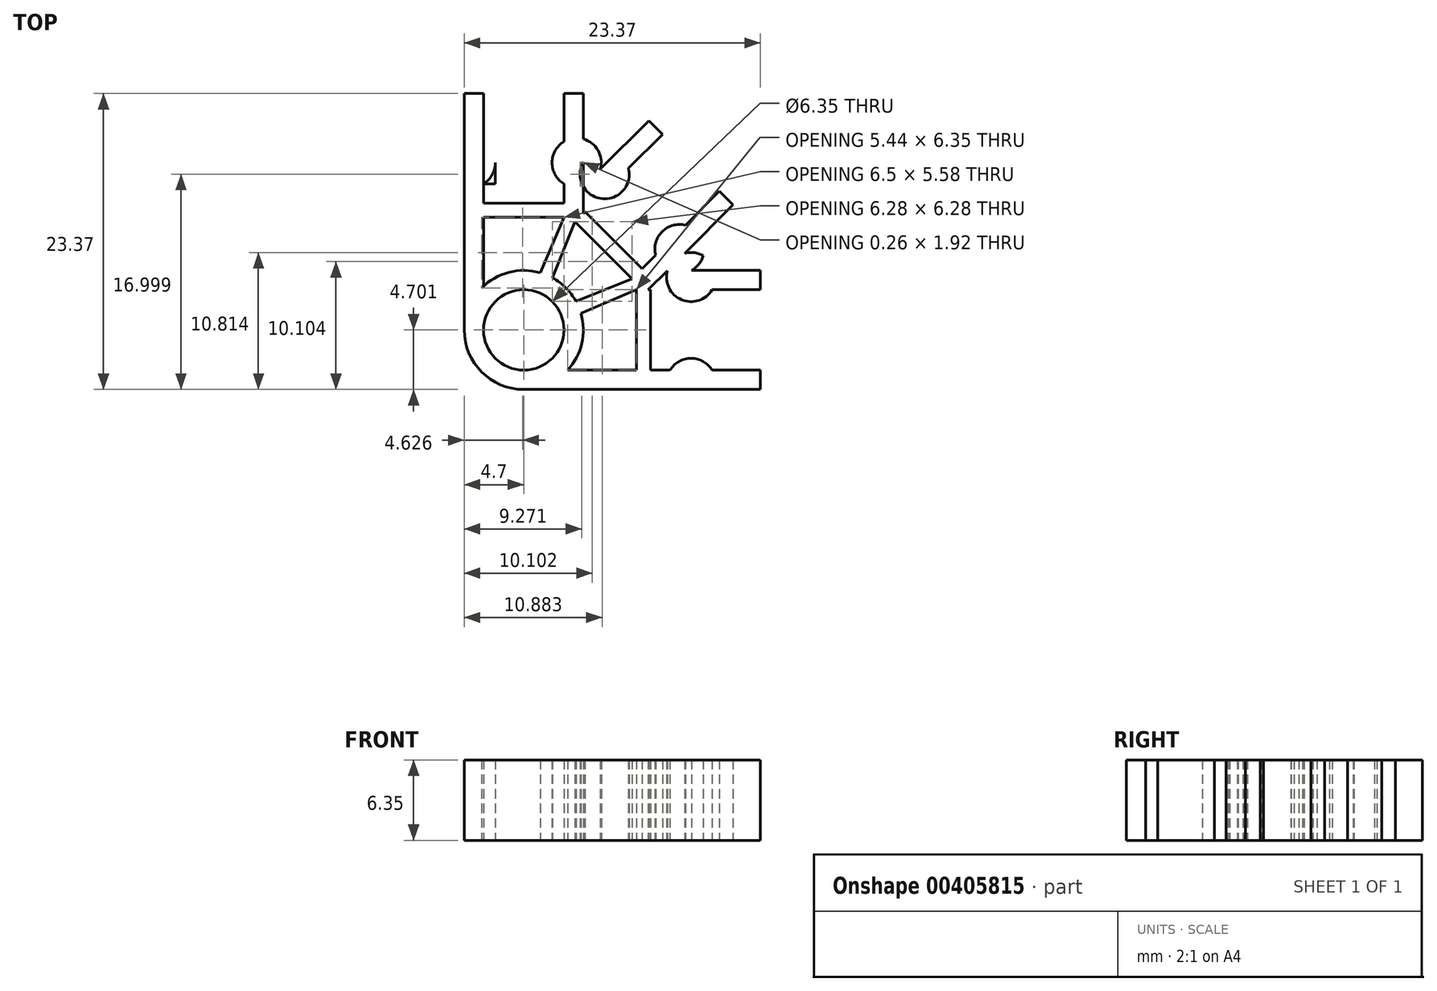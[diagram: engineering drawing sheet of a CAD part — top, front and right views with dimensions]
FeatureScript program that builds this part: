
annotation { "Feature Type Name" : "Feature", "Feature Type Description" : "" }
export const myFeature = defineFeature(function(context is Context, id is Id, definition is map)
    precondition{}
    {
        {
            var Q0;
            Q0=qCreatedBy(makeId("Top.planeOp"),FACE);
            var sketch = newSketch(context, id + "F0", { "sketchPlane" : qUnion([Q0])});
            skLineSegment(sketch, "E0", {"start": v(0, 8.65) * mm, "end": v(0, -8.65) * mm});
            skLineSegment(sketch, "E1.bottom", {"start": v(-3.17, 8.65) * mm, "end": v(3.18, 8.65) * mm});
            skLineSegment(sketch, "E1.top", {"start": v(-3.17, -8.65) * mm, "end": v(3.18, -8.65) * mm});
            skLineSegment(sketch, "E1.left", {"start": v(-3.18, 8.65) * mm, "end": v(-3.18, -8.65) * mm});
            skLineSegment(sketch, "E1.right", {"start": v(3.18, 8.65) * mm, "end": v(3.18, -8.65) * mm});
            skPoint(sketch, "E1.middle", {"position": v(0, 0) * mm});
            skLineSegment(sketch, "E2", {"start": v(-3.18, -7.12) * mm, "end": v(3.18, -7.12) * mm});
            skLineSegment(sketch, "E3", {"start": v(-3.18, -3.8) * mm, "end": v(3.18, -3.8) * mm});
            skLineSegment(sketch, "E4.bottom", {"start": v(-2.24, 8.65) * mm, "end": v(2.24, 8.65) * mm});
            skLineSegment(sketch, "E4.top", {"start": v(-2.24, -8.65) * mm, "end": v(2.24, -8.65) * mm});
            skLineSegment(sketch, "E4.left", {"start": v(-2.24, 8.65) * mm, "end": v(-2.24, -8.65) * mm});
            skLineSegment(sketch, "E4.right", {"start": v(2.24, 8.65) * mm, "end": v(2.24, -8.65) * mm});
            skCircle(sketch, "E5", {"center": v(4.18, -5.46) * mm, "radius": 1.94 * mm});
            skPoint(sketch, "E5.third.point", {"position": v(2.24, -5.46) * mm});
            skLineSegment(sketch, "E6.MirrorCS", {"start": v(3.17, -8.65) * mm, "end": v(-3.18, -8.65) * mm});
            skLineSegment(sketch, "E7.MirrorCS", {"start": v(3.17, 8.65) * mm, "end": v(-3.18, 8.65) * mm});
            skPoint(sketch, "E8.MirrorP", {"position": v(-2.24, -5.46) * mm});
            skLineSegment(sketch, "E9.MirrorCS", {"start": v(2.24, -8.65) * mm, "end": v(-2.24, -8.65) * mm});
            skLineSegment(sketch, "E10.MirrorCS", {"start": v(2.24, 8.65) * mm, "end": v(-2.24, 8.65) * mm});
            skLineSegment(sketch, "E11.MirrorCS", {"start": v(3.18, -7.12) * mm, "end": v(-3.18, -7.12) * mm});
            skLineSegment(sketch, "E12.MirrorCS", {"start": v(3.18, -3.8) * mm, "end": v(-3.18, -3.8) * mm});
            skCircle(sketch, "E13.MirrorC", {"center": v(-4.18, -5.46) * mm, "radius": 1.94 * mm});
            skLineSegment(sketch, "E14.MirrorCS", {"start": v(-3.18, 3.8) * mm, "end": v(3.18, 3.8) * mm});
            skLineSegment(sketch, "E15.MirrorCS", {"start": v(3.18, 7.12) * mm, "end": v(-3.18, 7.12) * mm});
            skLineSegment(sketch, "E16.MirrorCS", {"start": v(3.18, 3.8) * mm, "end": v(-3.18, 3.8) * mm});
            skLineSegment(sketch, "E17.MirrorCS", {"start": v(2.24, -8.65) * mm, "end": v(2.24, 8.65) * mm});
            skLineSegment(sketch, "E18.MirrorCS", {"start": v(-2.24, -8.65) * mm, "end": v(-2.24, 8.65) * mm});
            skLineSegment(sketch, "E19.MirrorCS", {"start": v(-3.18, 7.12) * mm, "end": v(3.17, 7.12) * mm});
            skLineSegment(sketch, "E20.MirrorCS", {"start": v(3.18, -8.65) * mm, "end": v(3.17, 8.65) * mm});
            skLineSegment(sketch, "E21.MirrorCS", {"start": v(0, -8.65) * mm, "end": v(0, 8.65) * mm});
            skLineSegment(sketch, "E22.MirrorCS", {"start": v(-3.18, -8.65) * mm, "end": v(-3.18, 8.65) * mm});
            skCircle(sketch, "E23.MirrorC", {"center": v(-4.18, 5.46) * mm, "radius": 1.94 * mm});
            skCircle(sketch, "E24.MirrorC", {"center": v(4.18, 5.46) * mm, "radius": 1.94 * mm});
            skLineSegment(sketch, "E25.MirrorCS", {"start": v(-3.17, -8.65) * mm, "end": v(-3.17, 8.65) * mm});
            skPoint(sketch, "E26.MirrorP", {"position": v(-2.24, 5.46) * mm});
            skLineSegment(sketch, "E27.MirrorCS", {"start": v(3.18, -8.65) * mm, "end": v(3.18, 8.65) * mm});
            skPoint(sketch, "E28.MirrorP", {"position": v(2.24, 5.46) * mm});
            skLineSegment(sketch, "E29.bottom", {"start": v(-4.7, 0) * mm, "end": v(4.7, 0) * mm});
            skLineSegment(sketch, "E29.top", {"start": v(-4.7, -23.37) * mm, "end": v(4.7, -23.37) * mm});
            skLineSegment(sketch, "E29.left", {"start": v(-4.7, 0) * mm, "end": v(-4.7, -23.37) * mm});
            skLineSegment(sketch, "E29.right", {"start": v(4.7, 0) * mm, "end": v(4.7, -23.37) * mm});
            skCircle(sketch, "E30", {"center": v(0, -18.67) * mm, "radius": 3.18 * mm});
            skCircle(sketch, "E31", {"center": v(0, -18.67) * mm, "radius": 4.7 * mm});
            skLineSegment(sketch, "E32", {"start": v(-4.7, -9.77) * mm, "end": v(4.7, -9.77) * mm});
            skLineSegment(sketch, "E33", {"start": v(3.18, -8.65) * mm, "end": v(3.18, -18.67) * mm});
            skLineSegment(sketch, "E34", {"start": v(-3.17, -8.65) * mm, "end": v(-3.17, -18.67) * mm});
            skLineSegment(sketch, "E35.1.0", {"start": v(9.88, -2.15) * mm, "end": v(16.52, -8.8) * mm});
            skLineSegment(sketch, "E35.1.1", {"start": v(9.88, -2.15) * mm, "end": v(-6.65, -18.67) * mm});
            skLineSegment(sketch, "E35.1.2", {"start": v(17.07, 2.9) * mm, "end": v(4.84, -9.34) * mm});
            skLineSegment(sketch, "E35.1.3", {"start": v(9.33, -13.83) * mm, "end": v(4.84, -9.34) * mm});
            skLineSegment(sketch, "E35.1.4", {"start": v(2.97, -9.05) * mm, "end": v(9.62, -15.7) * mm});
            skLineSegment(sketch, "E35.1.5", {"start": v(4.84, -9.34) * mm, "end": v(-2.25, -16.42) * mm});
            skLineSegment(sketch, "E35.1.6", {"start": v(9.33, -13.83) * mm, "end": v(2.25, -20.91) * mm});
            skLineSegment(sketch, "E35.1.9", {"start": v(16.52, -8.8) * mm, "end": v(0, -25.31) * mm});
            skLineSegment(sketch, "E35.1.10", {"start": v(21.56, -1.6) * mm, "end": v(9.33, -13.83) * mm});
            skLineSegment(sketch, "E35.2.0", {"start": v(18.67, -13.97) * mm, "end": v(18.67, -23.37) * mm});
            skLineSegment(sketch, "E35.2.1", {"start": v(18.67, -13.97) * mm, "end": v(-4.7, -13.97) * mm});
            skLineSegment(sketch, "E35.2.2", {"start": v(27.32, -15.5) * mm, "end": v(10.02, -15.5) * mm});
            skLineSegment(sketch, "E35.2.3", {"start": v(10.02, -21.84) * mm, "end": v(10.02, -15.5) * mm});
            skLineSegment(sketch, "E35.2.4", {"start": v(8.9, -13.97) * mm, "end": v(8.9, -23.37) * mm});
            skLineSegment(sketch, "E35.2.5", {"start": v(10.02, -15.5) * mm, "end": v(0, -15.5) * mm});
            skLineSegment(sketch, "E35.2.6", {"start": v(10.02, -21.84) * mm, "end": v(0, -21.84) * mm});
            skLineSegment(sketch, "E35.2.9", {"start": v(18.67, -23.37) * mm, "end": v(-4.7, -23.37) * mm});
            skLineSegment(sketch, "E35.2.10", {"start": v(27.32, -21.84) * mm, "end": v(10.02, -21.84) * mm});
            skLineSegment(sketch, "E35.anchor1", {"start": v(0, -18.67) * mm, "end": v(-4.7, 0) * mm, "construction": true});
            skLineSegment(sketch, "E35.anchor2", {"start": v(0, -18.67) * mm, "end": v(18.67, -13.97) * mm, "construction": true});
            skCircle(sketch, "E36", {"center": v(0, -18.67) * mm, "radius": 0.56 * mm});
            skLineSegment(sketch, "E37", {"start": v(3.17, -9.77) * mm, "end": v(-0.51, -18.45) * mm});
            skLineSegment(sketch, "E38", {"start": v(4.05, -10.13) * mm, "end": v(0.52, -18.88) * mm});
            skLineSegment(sketch, "E39", {"start": v(8.54, -14.62) * mm, "end": v(-0.2, -18.15) * mm});
            skLineSegment(sketch, "E40", {"start": v(8.9, -15.5) * mm, "end": v(0.22, -19.18) * mm});
            skCircle(sketch, "E41.1.0", {"center": v(6.39, -6.38) * mm, "radius": 1.94 * mm});
            skCircle(sketch, "E41.1.1", {"center": v(12.3, -12.28) * mm, "radius": 1.94 * mm});
            skCircle(sketch, "E41.2.0", {"center": v(13.2, -14.5) * mm, "radius": 1.94 * mm});
            skCircle(sketch, "E41.2.1", {"center": v(13.2, -22.85) * mm, "radius": 1.94 * mm});
            skLineSegment(sketch, "E41.anchor1", {"start": v(0, -18.67) * mm, "end": v(-4.18, -5.46) * mm, "construction": true});
            skLineSegment(sketch, "E41.anchor2", {"start": v(0, -18.67) * mm, "end": v(13.2, -14.5) * mm, "construction": true});
            skSolve(sketch);
        }
        {
            var Q0;
            {var subQ3=sQuery(id+"F0.wireOp",EDGE,"E30");var subQ7=sQuery(id+"F0.wireOp",EDGE,"E34");var subQ8=makeQuery(id+"F0.imprint","INTERSECT",VERTEX,{"derivedFrom":[subQ7,subQ3]});Q0=makeQuery(id+"F0.imprint","IMPRINT",FACE,{"disambiguationData":[TD([[makeQuery(id+"F0.imprint","IMPRINT",EDGE,{"disambiguationData":[TD([[subQ8,1.0]])],"derivedFrom":subQ7}),-1.0]])]});}
            var Q1;
            {var subQ4=sQuery(id+"F0.wireOp",EDGE,"E30");var subQ5=sQuery(id+"F0.wireOp",EDGE,"E34");var subQ6=makeQuery(id+"F0.imprint","INTERSECT",VERTEX,{"derivedFrom":[subQ5,subQ4]});Q1=makeQuery(id+"F0.imprint","IMPRINT",FACE,{"disambiguationData":[TD([[makeQuery(id+"F0.imprint","IMPRINT",EDGE,{"disambiguationData":[TD([[subQ6,1.0]])],"derivedFrom":subQ5}),1.0]])]});}
            var Q2;
            {var subQ0=sQuery(id+"F0.wireOp",EDGE,"E30");var subQ1=sQuery(id+"F0.wireOp",EDGE,"E35.1.5");var subQ2=makeQuery(id+"F0.imprint","INTERSECT",VERTEX,{"derivedFrom":[subQ1,subQ0]});Q2=makeQuery(id+"F0.imprint","IMPRINT",FACE,{"disambiguationData":[TD([[makeQuery(id+"F0.imprint","IMPRINT",EDGE,{"disambiguationData":[TD([[subQ2,1.0]])],"derivedFrom":subQ1}),1.0]])]});}
            var Q3;
            {var subQ0=sQuery(id+"F0.wireOp",EDGE,"E30");var subQ1=sQuery(id+"F0.wireOp",EDGE,"E35.2.5");var subQ2=makeQuery(id+"F0.imprint","INTERSECT",VERTEX,{"derivedFrom":[subQ1,subQ0]});Q3=makeQuery(id+"F0.imprint","IMPRINT",FACE,{"disambiguationData":[TD([[makeQuery(id+"F0.imprint","IMPRINT",EDGE,{"disambiguationData":[TD([[subQ2,1.0]])],"derivedFrom":subQ1}),1.0]])]});}
            var Q4;
            {var subQ0=sQuery(id+"F0.wireOp",EDGE,"E38");var subQ1=sQuery(id+"F0.wireOp",EDGE,"E35.2.5");var subQ2=makeQuery(id+"F0.imprint","INTERSECT",VERTEX,{"derivedFrom":[subQ1,subQ0]});Q4=makeQuery(id+"F0.imprint","IMPRINT",FACE,{"disambiguationData":[TD([[makeQuery(id+"F0.imprint","IMPRINT",EDGE,{"disambiguationData":[TD([[subQ2,-1.0]])],"derivedFrom":subQ1}),1.0]])]});}
            var Q5;
            {var subQ0=sQuery(id+"F0.wireOp",EDGE,"E38");var subQ1=sQuery(id+"F0.wireOp",EDGE,"E35.2.5");var subQ2=makeQuery(id+"F0.imprint","INTERSECT",VERTEX,{"derivedFrom":[subQ1,subQ0]});Q5=makeQuery(id+"F0.imprint","IMPRINT",FACE,{"disambiguationData":[TD([[makeQuery(id+"F0.imprint","IMPRINT",EDGE,{"disambiguationData":[TD([[subQ2,-1.0]])],"derivedFrom":subQ1}),-1.0]])]});}
            var Q6;
            {var subQ0=sQuery(id+"F0.wireOp",EDGE,"E31");var subQ1=sQuery(id+"F0.wireOp",EDGE,"E33");var subQ2=makeQuery(id+"F0.imprint","INTERSECT",VERTEX,{"derivedFrom":[subQ1,subQ0]});Q6=makeQuery(id+"F0.imprint","IMPRINT",FACE,{"disambiguationData":[TD([[makeQuery(id+"F0.imprint","IMPRINT",EDGE,{"disambiguationData":[TD([[subQ2,-1.0]])],"derivedFrom":subQ1}),-1.0]])]});}
            var Q7;
            {var subQ1=sQuery(id+"F0.wireOp",EDGE,"E35.2.5");var subQ7=sQuery(id+"F0.wireOp",EDGE,"E33");var subQ8=makeQuery(id+"F0.imprint","INTERSECT",VERTEX,{"derivedFrom":[subQ7,subQ1]});Q7=makeQuery(id+"F0.imprint","IMPRINT",FACE,{"disambiguationData":[TD([[makeQuery(id+"F0.imprint","IMPRINT",EDGE,{"disambiguationData":[TD([[subQ8,-1.0]])],"derivedFrom":subQ7}),-1.0]])]});}
            var Q8;
            {var subQ0=sQuery(id+"F0.wireOp",EDGE,"E35.2.5");var subQ1=sQuery(id+"F0.wireOp",EDGE,"E33");var subQ2=makeQuery(id+"F0.imprint","INTERSECT",VERTEX,{"derivedFrom":[subQ1,subQ0]});Q8=makeQuery(id+"F0.imprint","IMPRINT",FACE,{"disambiguationData":[TD([[makeQuery(id+"F0.imprint","IMPRINT",EDGE,{"disambiguationData":[TD([[subQ2,-1.0]])],"derivedFrom":subQ1}),1.0]])]});}
            var Q9;
            {var subQ0=sQuery(id+"F0.wireOp",EDGE,"E39");var subQ1=sQuery(id+"F0.wireOp",EDGE,"E33");var subQ2=makeQuery(id+"F0.imprint","INTERSECT",VERTEX,{"derivedFrom":[subQ1,subQ0]});Q9=makeQuery(id+"F0.imprint","IMPRINT",FACE,{"disambiguationData":[TD([[makeQuery(id+"F0.imprint","IMPRINT",EDGE,{"disambiguationData":[TD([[subQ2,-1.0]])],"derivedFrom":subQ1}),-1.0]])]});}
            var Q10;
            {var subQ0=sQuery(id+"F0.wireOp",EDGE,"E39");var subQ1=sQuery(id+"F0.wireOp",EDGE,"E33");var subQ2=makeQuery(id+"F0.imprint","INTERSECT",VERTEX,{"derivedFrom":[subQ1,subQ0]});Q10=makeQuery(id+"F0.imprint","IMPRINT",FACE,{"disambiguationData":[TD([[makeQuery(id+"F0.imprint","IMPRINT",EDGE,{"disambiguationData":[TD([[subQ2,-1.0]])],"derivedFrom":subQ1}),1.0]])]});}
            var Q11;
            {var subQ0=sQuery(id+"F0.wireOp",EDGE,"E31");var subQ1=sQuery(id+"F0.wireOp",EDGE,"E33");var subQ2=makeQuery(id+"F0.imprint","INTERSECT",VERTEX,{"derivedFrom":[subQ1,subQ0]});Q11=makeQuery(id+"F0.imprint","IMPRINT",FACE,{"disambiguationData":[TD([[makeQuery(id+"F0.imprint","IMPRINT",EDGE,{"disambiguationData":[TD([[subQ2,-1.0]])],"derivedFrom":subQ1}),1.0]])]});}
            var Q12;
            {var subQ0=sQuery(id+"F0.wireOp",EDGE,"E30");var subQ1=sQuery(id+"F0.wireOp",EDGE,"E33");var subQ2=makeQuery(id+"F0.imprint","INTERSECT",VERTEX,{"derivedFrom":[subQ1,subQ0]});Q12=makeQuery(id+"F0.imprint","IMPRINT",FACE,{"disambiguationData":[TD([[makeQuery(id+"F0.imprint","IMPRINT",EDGE,{"disambiguationData":[TD([[subQ2,1.0]])],"derivedFrom":subQ1}),1.0]])]});}
            var Q13;
            {var subQ0=sQuery(id+"F0.wireOp",EDGE,"E30");var subQ1=sQuery(id+"F0.wireOp",EDGE,"E33");var subQ2=makeQuery(id+"F0.imprint","INTERSECT",VERTEX,{"derivedFrom":[subQ1,subQ0]});Q13=makeQuery(id+"F0.imprint","IMPRINT",FACE,{"disambiguationData":[TD([[makeQuery(id+"F0.imprint","IMPRINT",EDGE,{"disambiguationData":[TD([[subQ2,1.0]])],"derivedFrom":subQ1}),-1.0]])]});}
            var Q14;
            {var subQ4=sQuery(id+"F0.wireOp",EDGE,"E30");var subQ5=sQuery(id+"F0.wireOp",EDGE,"E35.1.6");var subQ6=makeQuery(id+"F0.imprint","INTERSECT",VERTEX,{"derivedFrom":[subQ5,subQ4]});Q14=makeQuery(id+"F0.imprint","IMPRINT",FACE,{"disambiguationData":[TD([[makeQuery(id+"F0.imprint","IMPRINT",EDGE,{"disambiguationData":[TD([[subQ6,1.0]])],"derivedFrom":subQ5}),1.0]])]});}
            var Q15;
            {var subQ0=sQuery(id+"F0.wireOp",EDGE,"E35.1.1");var subQ1=sQuery(id+"F0.wireOp",EDGE,"E29.left");var subQ2=makeQuery(id+"F0.imprint","INTERSECT",VERTEX,{"derivedFrom":[subQ1,subQ0]});Q15=makeQuery(id+"F0.imprint","IMPRINT",FACE,{"disambiguationData":[TD([[makeQuery(id+"F0.imprint","IMPRINT",EDGE,{"disambiguationData":[TD([[subQ2,-1.0]])],"derivedFrom":subQ1}),1.0]])]});}
            var Q16;
            {var subQ1=sQuery(id+"F0.wireOp",EDGE,"E29.left");var subQ4=sQuery(id+"F0.wireOp",EDGE,"E35.2.1");var subQ8=makeQuery(id+"F0.imprint","INTERSECT",VERTEX,{"derivedFrom":[subQ1,subQ4]});Q16=makeQuery(id+"F0.imprint","IMPRINT",FACE,{"disambiguationData":[TD([[makeQuery(id+"F0.imprint","IMPRINT",EDGE,{"disambiguationData":[TD([[subQ8,-1.0]])],"derivedFrom":subQ1}),1.0]])]});}
            var Q17;
            {var subQ0=sQuery(id+"F0.wireOp",EDGE,"E32");var subQ1=sQuery(id+"F0.wireOp",EDGE,"E29.left");var subQ2=makeQuery(id+"F0.imprint","INTERSECT",VERTEX,{"derivedFrom":[subQ1,subQ0]});Q17=makeQuery(id+"F0.imprint","IMPRINT",FACE,{"disambiguationData":[TD([[makeQuery(id+"F0.imprint","IMPRINT",EDGE,{"disambiguationData":[TD([[subQ2,-1.0]])],"derivedFrom":subQ1}),1.0]])]});}
            var Q18;
            {var subQ0=sQuery(id+"F0.wireOp",EDGE,"E32");var subQ1=sQuery(id+"F0.wireOp",EDGE,"E29.left");var subQ2=makeQuery(id+"F0.imprint","INTERSECT",VERTEX,{"derivedFrom":[subQ1,subQ0]});Q18=makeQuery(id+"F0.imprint","IMPRINT",FACE,{"disambiguationData":[TD([[makeQuery(id+"F0.imprint","IMPRINT",EDGE,{"disambiguationData":[TD([[subQ2,1.0]])],"derivedFrom":subQ1}),1.0]])]});}
            var Q19;
            {var subQ0=sQuery(id+"F0.wireOp",EDGE,"E13.MirrorC");var subQ4=sQuery(id+"F0.wireOp",EDGE,"E29.left");var subQ5=makeQuery(id+"F0.imprint","INTERSECT",VERTEX,{"disambiguationData":[OD(0.0)],"derivedFrom":[subQ0,subQ4]});Q19=makeQuery(id+"F0.imprint","IMPRINT",FACE,{"disambiguationData":[TD([[makeQuery(id+"F0.imprint","IMPRINT",EDGE,{"disambiguationData":[TD([[subQ5,-1.0]])],"derivedFrom":subQ4}),1.0]])]});}
            var Q20;
            {var subQ3=sQuery(id+"F0.wireOp",EDGE,"E29.bottom");var subQ5=sQuery(id+"F0.wireOp",EDGE,"E29.left");var subQ6=makeQuery(id+"F0.imprint","INTERSECT",VERTEX,{"derivedFrom":[subQ3,subQ5]});Q20=makeQuery(id+"F0.imprint","IMPRINT",FACE,{"disambiguationData":[TD([[makeQuery(id+"F0.imprint","IMPRINT",EDGE,{"disambiguationData":[TD([[subQ6,-1.0]])],"derivedFrom":subQ3}),-1.0]])]});}
            var Q21;
            {var subQ0=sQuery(id+"F0.wireOp",EDGE,"E13.MirrorC");var subQ4=makeQuery(id+"F0.imprint","INTERSECT",VERTEX,{"derivedFrom":[sQuery(id+"F0.wireOp",EDGE,"E4.left"),subQ0]});Q21=makeQuery(id+"F0.imprint","IMPRINT",FACE,{"disambiguationData":[TD([[makeQuery(id+"F0.imprint","IMPRINT",EDGE,{"disambiguationData":[TD([[subQ4,1.0]])],"derivedFrom":subQ0}),-1.0]])]});}
            var Q22;
            {var subQ3=sQuery(id+"F0.wireOp",EDGE,"E29.right");var subQ5=sQuery(id+"F0.wireOp",EDGE,"E29.bottom");var subQ6=makeQuery(id+"F0.imprint","INTERSECT",VERTEX,{"derivedFrom":[subQ5,subQ3]});Q22=makeQuery(id+"F0.imprint","IMPRINT",FACE,{"disambiguationData":[TD([[makeQuery(id+"F0.imprint","IMPRINT",EDGE,{"disambiguationData":[TD([[subQ6,1.0]])],"derivedFrom":subQ5}),-1.0]])]});}
            var Q23;
            {var subQ0=sQuery(id+"F0.wireOp",EDGE,"E29.right");var subQ1=sQuery(id+"F0.wireOp",EDGE,"E5");var subQ2=makeQuery(id+"F0.imprint","INTERSECT",VERTEX,{"disambiguationData":[OD(0.0)],"derivedFrom":[subQ1,subQ0]});Q23=makeQuery(id+"F0.imprint","IMPRINT",FACE,{"disambiguationData":[TD([[makeQuery(id+"F0.imprint","IMPRINT",EDGE,{"disambiguationData":[TD([[subQ2,-1.0]])],"derivedFrom":subQ0}),-1.0]])]});}
            var Q24;
            {var subQ1=sQuery(id+"F0.wireOp",EDGE,"E5");var subQ3=makeQuery(id+"F0.imprint","INTERSECT",VERTEX,{"derivedFrom":[subQ1,sQuery(id+"F0.wireOp",EDGE,"E17.MirrorCS")]});Q24=makeQuery(id+"F0.imprint","IMPRINT",FACE,{"disambiguationData":[TD([[makeQuery(id+"F0.imprint","IMPRINT",EDGE,{"disambiguationData":[TD([[subQ3,1.0]])],"derivedFrom":subQ1}),1.0]])]});}
            var Q25;
            {var subQ0=sQuery(id+"F0.wireOp",EDGE,"E41.1.0");var subQ1=sQuery(id+"F0.wireOp",EDGE,"E29.right");var subQ2=makeQuery(id+"F0.imprint","INTERSECT",VERTEX,{"disambiguationData":[OD(0.0)],"derivedFrom":[subQ1,subQ0]});Q25=makeQuery(id+"F0.imprint","IMPRINT",FACE,{"disambiguationData":[TD([[makeQuery(id+"F0.imprint","IMPRINT",EDGE,{"disambiguationData":[TD([[subQ2,-1.0]])],"derivedFrom":subQ1}),-1.0]])]});}
            var Q26;
            {var subQ1=sQuery(id+"F0.wireOp",EDGE,"E5");var subQ3=sQuery(id+"F0.wireOp",EDGE,"E35.1.1");var subQ4=makeQuery(id+"F0.imprint","INTERSECT",VERTEX,{"disambiguationData":[OD(0.0)],"derivedFrom":[subQ1,subQ3]});Q26=makeQuery(id+"F0.imprint","IMPRINT",FACE,{"disambiguationData":[TD([[makeQuery(id+"F0.imprint","IMPRINT",EDGE,{"disambiguationData":[TD([[subQ4,-1.0]])],"derivedFrom":subQ3}),-1.0]])]});}
            var Q27;
            {var subQ1=sQuery(id+"F0.wireOp",EDGE,"E32");var subQ3=sQuery(id+"F0.wireOp",EDGE,"E35.1.4");var subQ4=makeQuery(id+"F0.imprint","INTERSECT",VERTEX,{"derivedFrom":[subQ1,subQ3]});Q27=makeQuery(id+"F0.imprint","IMPRINT",FACE,{"disambiguationData":[TD([[makeQuery(id+"F0.imprint","IMPRINT",EDGE,{"disambiguationData":[TD([[subQ4,1.0]])],"derivedFrom":subQ3}),-1.0]])]});}
            var Q28;
            {var subQ1=sQuery(id+"F0.wireOp",EDGE,"E32");var subQ3=sQuery(id+"F0.wireOp",EDGE,"E35.1.4");var subQ4=makeQuery(id+"F0.imprint","INTERSECT",VERTEX,{"derivedFrom":[subQ1,subQ3]});Q28=makeQuery(id+"F0.imprint","IMPRINT",FACE,{"disambiguationData":[TD([[makeQuery(id+"F0.imprint","IMPRINT",EDGE,{"disambiguationData":[TD([[subQ4,1.0]])],"derivedFrom":subQ1}),-1.0]])]});}
            var Q29;
            {var subQ0=sQuery(id+"F0.wireOp",EDGE,"E35.1.5");var subQ1=sQuery(id+"F0.wireOp",EDGE,"E33");var subQ2=makeQuery(id+"F0.imprint","INTERSECT",VERTEX,{"derivedFrom":[subQ1,subQ0]});Q29=makeQuery(id+"F0.imprint","IMPRINT",FACE,{"disambiguationData":[TD([[makeQuery(id+"F0.imprint","IMPRINT",EDGE,{"disambiguationData":[TD([[subQ2,-1.0]])],"derivedFrom":subQ1}),1.0]])]});}
            var Q30;
            {var subQ0=sQuery(id+"F0.wireOp",EDGE,"E35.1.1");var subQ1=sQuery(id+"F0.wireOp",EDGE,"E35.1.0");var subQ2=makeQuery(id+"F0.imprint","INTERSECT",VERTEX,{"derivedFrom":[subQ1,subQ0]});Q30=makeQuery(id+"F0.imprint","IMPRINT",FACE,{"disambiguationData":[TD([[makeQuery(id+"F0.imprint","IMPRINT",EDGE,{"disambiguationData":[TD([[subQ2,-1.0]])],"derivedFrom":subQ1}),-1.0]])]});}
            var Q31;
            {var subQ6=sQuery(id+"F0.wireOp",EDGE,"E5");var subQ8=sQuery(id+"F0.wireOp",EDGE,"E29.right");var subQ9=makeQuery(id+"F0.imprint","INTERSECT",VERTEX,{"disambiguationData":[OD(1.0)],"derivedFrom":[subQ6,subQ8]});Q31=makeQuery(id+"F0.imprint","IMPRINT",FACE,{"disambiguationData":[TD([[makeQuery(id+"F0.imprint","IMPRINT",EDGE,{"disambiguationData":[TD([[subQ9,-1.0]])],"derivedFrom":subQ6}),-1.0]])]});}
            var Q32;
            {var subQ0=sQuery(id+"F0.wireOp",EDGE,"E41.1.0");var subQ1=sQuery(id+"F0.wireOp",EDGE,"E35.1.2");var subQ2=makeQuery(id+"F0.imprint","INTERSECT",VERTEX,{"disambiguationData":[OD(0.0)],"derivedFrom":[subQ1,subQ0]});Q32=makeQuery(id+"F0.imprint","IMPRINT",FACE,{"disambiguationData":[TD([[makeQuery(id+"F0.imprint","IMPRINT",EDGE,{"disambiguationData":[TD([[subQ2,-1.0]])],"derivedFrom":subQ1}),1.0]])]});}
            var Q33;
            {var subQ0=sQuery(id+"F0.wireOp",EDGE,"E35.1.9");var subQ1=sQuery(id+"F0.wireOp",EDGE,"E35.1.0");var subQ2=makeQuery(id+"F0.imprint","INTERSECT",VERTEX,{"derivedFrom":[subQ1,subQ0]});Q33=makeQuery(id+"F0.imprint","IMPRINT",FACE,{"disambiguationData":[TD([[makeQuery(id+"F0.imprint","IMPRINT",EDGE,{"disambiguationData":[TD([[subQ2,1.0]])],"derivedFrom":subQ1}),-1.0]])]});}
            var Q34;
            {var subQ3=sQuery(id+"F0.wireOp",EDGE,"E41.1.1");var subQ8=sQuery(id+"F0.wireOp",EDGE,"E35.1.9");var subQ9=makeQuery(id+"F0.imprint","INTERSECT",VERTEX,{"disambiguationData":[OD(0.0)],"derivedFrom":[subQ8,subQ3]});Q34=makeQuery(id+"F0.imprint","IMPRINT",FACE,{"disambiguationData":[TD([[makeQuery(id+"F0.imprint","IMPRINT",EDGE,{"disambiguationData":[TD([[subQ9,-1.0]])],"derivedFrom":subQ8}),-1.0]])]});}
            var Q35;
            {var subQ0=sQuery(id+"F0.wireOp",EDGE,"E41.1.1");var subQ1=sQuery(id+"F0.wireOp",EDGE,"E35.1.10");var subQ2=makeQuery(id+"F0.imprint","INTERSECT",VERTEX,{"disambiguationData":[OD(0.0)],"derivedFrom":[subQ1,subQ0]});Q35=makeQuery(id+"F0.imprint","IMPRINT",FACE,{"disambiguationData":[TD([[makeQuery(id+"F0.imprint","IMPRINT",EDGE,{"disambiguationData":[TD([[subQ2,-1.0]])],"derivedFrom":subQ1}),-1.0]])]});}
            var Q36;
            {var subQ0=sQuery(id+"F0.wireOp",EDGE,"E41.1.0");var subQ1=sQuery(id+"F0.wireOp",EDGE,"E29.right");var subQ2=makeQuery(id+"F0.imprint","INTERSECT",VERTEX,{"disambiguationData":[OD(1.0)],"derivedFrom":[subQ1,subQ0]});Q36=makeQuery(id+"F0.imprint","IMPRINT",FACE,{"disambiguationData":[TD([[makeQuery(id+"F0.imprint","IMPRINT",EDGE,{"disambiguationData":[TD([[subQ2,-1.0]])],"derivedFrom":subQ1}),1.0]])]});}
            var Q37;
            {var subQ0=sQuery(id+"F0.wireOp",EDGE,"E29.right");var subQ1=sQuery(id+"F0.wireOp",EDGE,"E5");var subQ2=makeQuery(id+"F0.imprint","INTERSECT",VERTEX,{"disambiguationData":[OD(1.0)],"derivedFrom":[subQ1,subQ0]});Q37=makeQuery(id+"F0.imprint","IMPRINT",FACE,{"disambiguationData":[TD([[makeQuery(id+"F0.imprint","IMPRINT",EDGE,{"disambiguationData":[TD([[subQ2,-1.0]])],"derivedFrom":subQ1}),1.0]])]});}
            var Q38;
            {var subQ0=sQuery(id+"F0.wireOp",EDGE,"E41.2.0");var subQ1=sQuery(id+"F0.wireOp",EDGE,"E35.1.9");var subQ2=makeQuery(id+"F0.imprint","INTERSECT",VERTEX,{"disambiguationData":[OD(0.0)],"derivedFrom":[subQ1,subQ0]});Q38=makeQuery(id+"F0.imprint","IMPRINT",FACE,{"disambiguationData":[TD([[makeQuery(id+"F0.imprint","IMPRINT",EDGE,{"disambiguationData":[TD([[subQ2,-1.0]])],"derivedFrom":subQ1}),-1.0]])]});}
            var Q39;
            {var subQ0=sQuery(id+"F0.wireOp",EDGE,"E41.2.0");var subQ1=sQuery(id+"F0.wireOp",EDGE,"E35.2.2");var subQ2=makeQuery(id+"F0.imprint","INTERSECT",VERTEX,{"disambiguationData":[OD(0.0)],"derivedFrom":[subQ1,subQ0]});Q39=makeQuery(id+"F0.imprint","IMPRINT",FACE,{"disambiguationData":[TD([[makeQuery(id+"F0.imprint","IMPRINT",EDGE,{"disambiguationData":[TD([[subQ2,-1.0]])],"derivedFrom":subQ1}),1.0]])]});}
            var Q40;
            {var subQ0=sQuery(id+"F0.wireOp",EDGE,"E41.1.1");var subQ1=sQuery(id+"F0.wireOp",EDGE,"E35.1.9");var subQ2=makeQuery(id+"F0.imprint","INTERSECT",VERTEX,{"disambiguationData":[OD(1.0)],"derivedFrom":[subQ1,subQ0]});Q40=makeQuery(id+"F0.imprint","IMPRINT",FACE,{"disambiguationData":[TD([[makeQuery(id+"F0.imprint","IMPRINT",EDGE,{"disambiguationData":[TD([[subQ2,-1.0]])],"derivedFrom":subQ1}),1.0]])]});}
            var Q41;
            {var subQ0=sQuery(id+"F0.wireOp",EDGE,"E35.2.1");var subQ1=sQuery(id+"F0.wireOp",EDGE,"E35.2.0");var subQ2=makeQuery(id+"F0.imprint","INTERSECT",VERTEX,{"derivedFrom":[subQ1,subQ0]});Q41=makeQuery(id+"F0.imprint","IMPRINT",FACE,{"disambiguationData":[TD([[makeQuery(id+"F0.imprint","IMPRINT",EDGE,{"disambiguationData":[TD([[subQ2,-1.0]])],"derivedFrom":subQ1}),-1.0]])]});}
            var Q42;
            {var subQ0=sQuery(id+"F0.wireOp",EDGE,"E41.2.0");var subQ1=sQuery(id+"F0.wireOp",EDGE,"E35.1.9");var subQ2=makeQuery(id+"F0.imprint","INTERSECT",VERTEX,{"disambiguationData":[OD(1.0)],"derivedFrom":[subQ1,subQ0]});Q42=makeQuery(id+"F0.imprint","IMPRINT",FACE,{"disambiguationData":[TD([[makeQuery(id+"F0.imprint","IMPRINT",EDGE,{"disambiguationData":[TD([[subQ2,-1.0]])],"derivedFrom":subQ1}),1.0]])]});}
            var Q43;
            {var subQ0=sQuery(id+"F0.wireOp",EDGE,"E41.2.1");var subQ1=sQuery(id+"F0.wireOp",EDGE,"E35.2.10");var subQ2=makeQuery(id+"F0.imprint","INTERSECT",VERTEX,{"disambiguationData":[OD(0.0)],"derivedFrom":[subQ1,subQ0]});Q43=makeQuery(id+"F0.imprint","IMPRINT",FACE,{"disambiguationData":[TD([[makeQuery(id+"F0.imprint","IMPRINT",EDGE,{"disambiguationData":[TD([[subQ2,-1.0]])],"derivedFrom":subQ1}),-1.0]])]});}
            var Q44;
            {var subQ5=sQuery(id+"F0.wireOp",EDGE,"E35.2.4");var subQ7=sQuery(id+"F0.wireOp",EDGE,"E35.2.9");var subQ8=makeQuery(id+"F0.imprint","INTERSECT",VERTEX,{"derivedFrom":[subQ5,subQ7]});Q44=makeQuery(id+"F0.imprint","IMPRINT",FACE,{"disambiguationData":[TD([[makeQuery(id+"F0.imprint","IMPRINT",EDGE,{"disambiguationData":[TD([[subQ8,1.0]])],"derivedFrom":subQ5}),1.0]])]});}
            var Q45;
            {var subQ0=sQuery(id+"F0.wireOp",EDGE,"E41.2.1");var subQ1=sQuery(id+"F0.wireOp",EDGE,"E35.2.9");var subQ2=makeQuery(id+"F0.imprint","INTERSECT",VERTEX,{"disambiguationData":[OD(0.0)],"derivedFrom":[subQ1,subQ0]});Q45=makeQuery(id+"F0.imprint","IMPRINT",FACE,{"disambiguationData":[TD([[makeQuery(id+"F0.imprint","IMPRINT",EDGE,{"disambiguationData":[TD([[subQ2,-1.0]])],"derivedFrom":subQ1}),-1.0]])]});}
            var Q46;
            {var subQ0=sQuery(id+"F0.wireOp",EDGE,"E35.2.9");var subQ1=sQuery(id+"F0.wireOp",EDGE,"E35.2.0");var subQ2=makeQuery(id+"F0.imprint","INTERSECT",VERTEX,{"derivedFrom":[subQ1,subQ0]});Q46=makeQuery(id+"F0.imprint","IMPRINT",FACE,{"disambiguationData":[TD([[makeQuery(id+"F0.imprint","IMPRINT",EDGE,{"disambiguationData":[TD([[subQ2,1.0]])],"derivedFrom":subQ1}),-1.0]])]});}
            var Q47;
            {var subQ0=sQuery(id+"F0.wireOp",EDGE,"E35.2.9");var subQ1=sQuery(id+"F0.wireOp",EDGE,"E35.1.9");var subQ2=makeQuery(id+"F0.imprint","INTERSECT",VERTEX,{"derivedFrom":[subQ1,subQ0]});Q47=makeQuery(id+"F0.imprint","IMPRINT",FACE,{"disambiguationData":[TD([[makeQuery(id+"F0.imprint","IMPRINT",EDGE,{"disambiguationData":[TD([[subQ2,1.0]])],"derivedFrom":subQ1}),-1.0]])]});}
            var Q48;
            {var subQ0=sQuery(id+"F0.wireOp",EDGE,"E35.2.9");var subQ6=sQuery(id+"F0.wireOp",EDGE,"E29.right");var subQ7=makeQuery(id+"F0.imprint","INTERSECT",VERTEX,{"derivedFrom":[subQ6,subQ0]});Q48=makeQuery(id+"F0.imprint","IMPRINT",FACE,{"disambiguationData":[TD([[makeQuery(id+"F0.imprint","IMPRINT",EDGE,{"disambiguationData":[TD([[subQ7,1.0]])],"derivedFrom":subQ6}),-1.0]])]});}
            var Q49;
            {var subQ0=sQuery(id+"F0.wireOp",EDGE,"E35.2.9");var subQ1=sQuery(id+"F0.wireOp",EDGE,"E29.right");var subQ2=makeQuery(id+"F0.imprint","INTERSECT",VERTEX,{"derivedFrom":[subQ1,subQ0]});Q49=makeQuery(id+"F0.imprint","IMPRINT",FACE,{"disambiguationData":[TD([[makeQuery(id+"F0.imprint","IMPRINT",EDGE,{"disambiguationData":[TD([[subQ2,1.0]])],"derivedFrom":subQ1}),1.0]])]});}
            var Q50;
            {var subQ9=sQuery(id+"F0.wireOp",EDGE,"E5");var subQ11=sQuery(id+"F0.wireOp",EDGE,"E35.1.1");var subQ15=makeQuery(id+"F0.imprint","INTERSECT",VERTEX,{"disambiguationData":[OD(0.0)],"derivedFrom":[subQ9,subQ11]});Q50=makeQuery(id+"F0.imprint","IMPRINT",FACE,{"disambiguationData":[TD([[makeQuery(id+"F0.imprint","IMPRINT",EDGE,{"disambiguationData":[TD([[subQ15,-1.0]])],"derivedFrom":subQ9}),-1.0]])]});}
            var Q51;
            {var subQ0=sQuery(id+"F0.wireOp",EDGE,"E35.1.4");var subQ1=sQuery(id+"F0.wireOp",EDGE,"E32");var subQ2=makeQuery(id+"F0.imprint","INTERSECT",VERTEX,{"derivedFrom":[subQ1,subQ0]});Q51=makeQuery(id+"F0.imprint","IMPRINT",FACE,{"disambiguationData":[TD([[makeQuery(id+"F0.imprint","IMPRINT",EDGE,{"disambiguationData":[TD([[subQ2,-1.0]])],"derivedFrom":subQ1}),-1.0]])]});}
            var Q52;
            {var subQ1=sQuery(id+"F0.wireOp",EDGE,"E33");var subQ3=sQuery(id+"F0.wireOp",EDGE,"E35.1.5");var subQ4=makeQuery(id+"F0.imprint","INTERSECT",VERTEX,{"derivedFrom":[subQ1,subQ3]});Q52=makeQuery(id+"F0.imprint","IMPRINT",FACE,{"disambiguationData":[TD([[makeQuery(id+"F0.imprint","IMPRINT",EDGE,{"disambiguationData":[TD([[subQ4,-1.0]])],"derivedFrom":subQ3}),-1.0]])]});}
            var Q53;
            {var subQ1=sQuery(id+"F0.wireOp",EDGE,"E35.1.5");var subQ5=sQuery(id+"F0.wireOp",EDGE,"E33");var subQ6=makeQuery(id+"F0.imprint","INTERSECT",VERTEX,{"derivedFrom":[subQ5,subQ1]});Q53=makeQuery(id+"F0.imprint","IMPRINT",FACE,{"disambiguationData":[TD([[makeQuery(id+"F0.imprint","IMPRINT",EDGE,{"disambiguationData":[TD([[subQ6,-1.0]])],"derivedFrom":subQ5}),-1.0]])]});}
            var Q54;
            {var subQ0=sQuery(id+"F0.wireOp",EDGE,"E38");var subQ1=sQuery(id+"F0.wireOp",EDGE,"E35.2.1");var subQ2=makeQuery(id+"F0.imprint","INTERSECT",VERTEX,{"derivedFrom":[subQ1,subQ0]});Q54=makeQuery(id+"F0.imprint","IMPRINT",FACE,{"disambiguationData":[TD([[makeQuery(id+"F0.imprint","IMPRINT",EDGE,{"disambiguationData":[TD([[subQ2,-1.0]])],"derivedFrom":subQ1}),1.0]])]});}
            var Q55;
            {var subQ1=sQuery(id+"F0.wireOp",EDGE,"E35.1.6");var subQ3=sQuery(id+"F0.wireOp",EDGE,"E35.2.1");var subQ4=makeQuery(id+"F0.imprint","INTERSECT",VERTEX,{"derivedFrom":[subQ1,subQ3]});Q55=makeQuery(id+"F0.imprint","IMPRINT",FACE,{"disambiguationData":[TD([[makeQuery(id+"F0.imprint","IMPRINT",EDGE,{"disambiguationData":[TD([[subQ4,1.0]])],"derivedFrom":subQ3}),-1.0]])]});}
            var Q56;
            {var subQ10=sQuery(id+"F0.wireOp",EDGE,"E35.2.4");var subQ12=sQuery(id+"F0.wireOp",EDGE,"E35.1.4");var subQ13=makeQuery(id+"F0.imprint","INTERSECT",VERTEX,{"derivedFrom":[subQ12,subQ10]});Q56=makeQuery(id+"F0.imprint","IMPRINT",FACE,{"disambiguationData":[TD([[makeQuery(id+"F0.imprint","IMPRINT",EDGE,{"disambiguationData":[TD([[subQ13,-1.0]])],"derivedFrom":subQ12}),1.0]])]});}
            var Q57;
            {var subQ0=sQuery(id+"F0.wireOp",EDGE,"E35.2.1");var subQ1=sQuery(id+"F0.wireOp",EDGE,"E35.1.9");var subQ2=makeQuery(id+"F0.imprint","INTERSECT",VERTEX,{"derivedFrom":[subQ1,subQ0]});Q57=makeQuery(id+"F0.imprint","IMPRINT",FACE,{"disambiguationData":[TD([[makeQuery(id+"F0.imprint","IMPRINT",EDGE,{"disambiguationData":[TD([[subQ2,-1.0]])],"derivedFrom":subQ1}),1.0]])]});}
            var Q58;
            {var subQ0=sQuery(id+"F0.wireOp",EDGE,"E35.2.4");var subQ1=sQuery(id+"F0.wireOp",EDGE,"E35.1.4");var subQ2=makeQuery(id+"F0.imprint","INTERSECT",VERTEX,{"derivedFrom":[subQ1,subQ0]});Q58=makeQuery(id+"F0.imprint","IMPRINT",FACE,{"disambiguationData":[TD([[makeQuery(id+"F0.imprint","IMPRINT",EDGE,{"disambiguationData":[TD([[subQ2,-1.0]])],"derivedFrom":subQ1}),-1.0]])]});}
            var Q59;
            {var subQ1=sQuery(id+"F0.wireOp",EDGE,"E35.1.4");var subQ3=sQuery(id+"F0.wireOp",EDGE,"E35.2.4");var subQ4=makeQuery(id+"F0.imprint","INTERSECT",VERTEX,{"derivedFrom":[subQ1,subQ3]});Q59=makeQuery(id+"F0.imprint","IMPRINT",FACE,{"disambiguationData":[TD([[makeQuery(id+"F0.imprint","IMPRINT",EDGE,{"disambiguationData":[TD([[subQ4,1.0]])],"derivedFrom":subQ3}),-1.0]])]});}
            var Q60;
            {var subQ1=sQuery(id+"F0.wireOp",EDGE,"E35.1.4");var subQ3=sQuery(id+"F0.wireOp",EDGE,"E35.2.4");var subQ4=makeQuery(id+"F0.imprint","INTERSECT",VERTEX,{"derivedFrom":[subQ1,subQ3]});Q60=makeQuery(id+"F0.imprint","IMPRINT",FACE,{"disambiguationData":[TD([[makeQuery(id+"F0.imprint","IMPRINT",EDGE,{"disambiguationData":[TD([[subQ4,1.0]])],"derivedFrom":subQ1}),-1.0]])]});}
            var Q61;
            {var subQ1=sQuery(id+"F0.wireOp",EDGE,"E35.1.6");var subQ3=sQuery(id+"F0.wireOp",EDGE,"E35.2.5");var subQ4=makeQuery(id+"F0.imprint","INTERSECT",VERTEX,{"derivedFrom":[subQ1,subQ3]});Q61=makeQuery(id+"F0.imprint","IMPRINT",FACE,{"disambiguationData":[TD([[makeQuery(id+"F0.imprint","IMPRINT",EDGE,{"disambiguationData":[TD([[subQ4,-1.0]])],"derivedFrom":subQ3}),-1.0]])]});}
            var Q62;
            {var subQ0=sQuery(id+"F0.wireOp",EDGE,"E35.2.5");var subQ1=sQuery(id+"F0.wireOp",EDGE,"E35.1.6");var subQ2=makeQuery(id+"F0.imprint","INTERSECT",VERTEX,{"derivedFrom":[subQ1,subQ0]});Q62=makeQuery(id+"F0.imprint","IMPRINT",FACE,{"disambiguationData":[TD([[makeQuery(id+"F0.imprint","IMPRINT",EDGE,{"disambiguationData":[TD([[subQ2,-1.0]])],"derivedFrom":subQ1}),1.0]])]});}
            var Q63;
            {var subQ0=sQuery(id+"F0.wireOp",EDGE,"E39");var subQ1=sQuery(id+"F0.wireOp",EDGE,"E29.right");var subQ2=makeQuery(id+"F0.imprint","INTERSECT",VERTEX,{"derivedFrom":[subQ1,subQ0]});Q63=makeQuery(id+"F0.imprint","IMPRINT",FACE,{"disambiguationData":[TD([[makeQuery(id+"F0.imprint","IMPRINT",EDGE,{"disambiguationData":[TD([[subQ2,-1.0]])],"derivedFrom":subQ1}),1.0]])]});}
            var Q64;
            {var subQ0=sQuery(id+"F0.wireOp",EDGE,"E39");var subQ1=sQuery(id+"F0.wireOp",EDGE,"E29.right");var subQ2=makeQuery(id+"F0.imprint","INTERSECT",VERTEX,{"derivedFrom":[subQ1,subQ0]});Q64=makeQuery(id+"F0.imprint","IMPRINT",FACE,{"disambiguationData":[TD([[makeQuery(id+"F0.imprint","IMPRINT",EDGE,{"disambiguationData":[TD([[subQ2,-1.0]])],"derivedFrom":subQ1}),-1.0]])]});}
            var Q65;
            {var subQ3=sQuery(id+"F0.wireOp",EDGE,"E35.1.1");var subQ5=sQuery(id+"F0.wireOp",EDGE,"E35.1.4");var subQ6=makeQuery(id+"F0.imprint","INTERSECT",VERTEX,{"derivedFrom":[subQ3,subQ5]});Q65=makeQuery(id+"F0.imprint","IMPRINT",FACE,{"disambiguationData":[TD([[makeQuery(id+"F0.imprint","IMPRINT",EDGE,{"disambiguationData":[TD([[subQ6,-1.0]])],"derivedFrom":subQ3}),1.0]])]});}
            var Q66;
            {var subQ0=sQuery(id+"F0.wireOp",EDGE,"E35.1.1");var subQ1=sQuery(id+"F0.wireOp",EDGE,"E33");var subQ2=makeQuery(id+"F0.imprint","INTERSECT",VERTEX,{"derivedFrom":[subQ1,subQ0]});Q66=makeQuery(id+"F0.imprint","IMPRINT",FACE,{"disambiguationData":[TD([[makeQuery(id+"F0.imprint","IMPRINT",EDGE,{"disambiguationData":[TD([[subQ2,-1.0]])],"derivedFrom":subQ1}),-1.0]])]});}
            var Q67;
            {var subQ7=sQuery(id+"F0.wireOp",EDGE,"E34");var subQ9=sQuery(id+"F0.wireOp",EDGE,"E32");var subQ10=makeQuery(id+"F0.imprint","INTERSECT",VERTEX,{"derivedFrom":[subQ9,subQ7]});Q67=makeQuery(id+"F0.imprint","IMPRINT",FACE,{"disambiguationData":[TD([[makeQuery(id+"F0.imprint","IMPRINT",EDGE,{"disambiguationData":[TD([[subQ10,-1.0]])],"derivedFrom":subQ9}),1.0]])]});}
            var Q68;
            {var subQ0=sQuery(id+"F0.wireOp",EDGE,"E32");var subQ1=sQuery(id+"F0.wireOp",EDGE,"E29.right");var subQ2=makeQuery(id+"F0.imprint","INTERSECT",VERTEX,{"derivedFrom":[subQ1,subQ0]});Q68=makeQuery(id+"F0.imprint","IMPRINT",FACE,{"disambiguationData":[TD([[makeQuery(id+"F0.imprint","IMPRINT",EDGE,{"disambiguationData":[TD([[subQ2,1.0]])],"derivedFrom":subQ1}),-1.0]])]});}
            var Q69;
            {var subQ0=sQuery(id+"F0.wireOp",EDGE,"E32");var subQ1=sQuery(id+"F0.wireOp",EDGE,"E29.right");var subQ2=makeQuery(id+"F0.imprint","INTERSECT",VERTEX,{"derivedFrom":[subQ1,subQ0]});Q69=makeQuery(id+"F0.imprint","IMPRINT",FACE,{"disambiguationData":[TD([[makeQuery(id+"F0.imprint","IMPRINT",EDGE,{"disambiguationData":[TD([[subQ2,-1.0]])],"derivedFrom":subQ1}),-1.0]])]});}
            var Q70;
            {var subQ6=sQuery(id+"F0.wireOp",EDGE,"E35.1.3");Q70=makeQuery(id+"F0.imprint","IMPRINT",FACE,{"disambiguationData":[TD([[makeQuery(id+"F0.imprint","IMPRINT",EDGE,{"derivedFrom":subQ6}),1.0]])]});}
            var Q71;
            {var subQ3=sQuery(id+"F0.wireOp",EDGE,"E35.2.1");var subQ5=sQuery(id+"F0.wireOp",EDGE,"E35.2.4");var subQ6=makeQuery(id+"F0.imprint","INTERSECT",VERTEX,{"derivedFrom":[subQ3,subQ5]});Q71=makeQuery(id+"F0.imprint","IMPRINT",FACE,{"disambiguationData":[TD([[makeQuery(id+"F0.imprint","IMPRINT",EDGE,{"disambiguationData":[TD([[subQ6,-1.0]])],"derivedFrom":subQ3}),1.0]])]});}
            var Q72;
            {var subQ0=sQuery(id+"F0.wireOp",EDGE,"E35.2.1");var subQ1=sQuery(id+"F0.wireOp",EDGE,"E35.1.6");var subQ2=makeQuery(id+"F0.imprint","INTERSECT",VERTEX,{"derivedFrom":[subQ1,subQ0]});Q72=makeQuery(id+"F0.imprint","IMPRINT",FACE,{"disambiguationData":[TD([[makeQuery(id+"F0.imprint","IMPRINT",EDGE,{"disambiguationData":[TD([[subQ2,-1.0]])],"derivedFrom":subQ1}),-1.0]])]});}
            var Q73;
            {var subQ5=sQuery(id+"F0.wireOp",EDGE,"E35.2.3");Q73=makeQuery(id+"F0.imprint","IMPRINT",FACE,{"disambiguationData":[TD([[makeQuery(id+"F0.imprint","IMPRINT",EDGE,{"derivedFrom":subQ5}),1.0]])]});}
            var Q74;
            {var subQ0=sQuery(id+"F0.wireOp",EDGE,"E35.1.9");var subQ1=sQuery(id+"F0.wireOp",EDGE,"E35.1.4");var subQ2=makeQuery(id+"F0.imprint","INTERSECT",VERTEX,{"derivedFrom":[subQ1,subQ0]});Q74=makeQuery(id+"F0.imprint","IMPRINT",FACE,{"disambiguationData":[TD([[makeQuery(id+"F0.imprint","IMPRINT",EDGE,{"disambiguationData":[TD([[subQ2,1.0]])],"derivedFrom":subQ1}),-1.0]])]});}
            var Q75;
            {var subQ0=sQuery(id+"F0.wireOp",EDGE,"E35.1.9");var subQ1=sQuery(id+"F0.wireOp",EDGE,"E35.1.4");var subQ2=makeQuery(id+"F0.imprint","INTERSECT",VERTEX,{"derivedFrom":[subQ1,subQ0]});Q75=makeQuery(id+"F0.imprint","IMPRINT",FACE,{"disambiguationData":[TD([[makeQuery(id+"F0.imprint","IMPRINT",EDGE,{"disambiguationData":[TD([[subQ2,1.0]])],"derivedFrom":subQ1}),1.0]])]});}
            var Q76;
            {var subQ0=sQuery(id+"F0.wireOp",EDGE,"E41.1.0");var subQ1=sQuery(id+"F0.wireOp",EDGE,"E5");var subQ2=makeQuery(id+"F0.imprint","INTERSECT",VERTEX,{"disambiguationData":[OD(1.0)],"derivedFrom":[subQ1,subQ0]});Q76=makeQuery(id+"F0.imprint","IMPRINT",FACE,{"disambiguationData":[TD([[makeQuery(id+"F0.imprint","IMPRINT",EDGE,{"disambiguationData":[TD([[subQ2,-1.0]])],"derivedFrom":subQ1}),-1.0]])]});}
            var Q77;
            {var subQ0=sQuery(id+"F0.wireOp",EDGE,"E35.1.1");var subQ1=sQuery(id+"F0.wireOp",EDGE,"E5");var subQ2=makeQuery(id+"F0.imprint","INTERSECT",VERTEX,{"disambiguationData":[OD(0.0)],"derivedFrom":[subQ1,subQ0]});Q77=makeQuery(id+"F0.imprint","IMPRINT",FACE,{"disambiguationData":[TD([[makeQuery(id+"F0.imprint","IMPRINT",EDGE,{"disambiguationData":[TD([[subQ2,-1.0]])],"derivedFrom":subQ1}),1.0]])]});}
            var Q78;
            {var subQ0=sQuery(id+"F0.wireOp",EDGE,"E41.1.0");var subQ1=sQuery(id+"F0.wireOp",EDGE,"E5");var subQ2=makeQuery(id+"F0.imprint","INTERSECT",VERTEX,{"disambiguationData":[OD(1.0)],"derivedFrom":[subQ1,subQ0]});Q78=makeQuery(id+"F0.imprint","IMPRINT",FACE,{"disambiguationData":[TD([[makeQuery(id+"F0.imprint","IMPRINT",EDGE,{"disambiguationData":[TD([[subQ2,-1.0]])],"derivedFrom":subQ1}),1.0]])]});}
            var Q79;
            {var subQ0=sQuery(id+"F0.wireOp",EDGE,"E41.1.1");var subQ1=sQuery(id+"F0.wireOp",EDGE,"E35.1.9");var subQ2=makeQuery(id+"F0.imprint","INTERSECT",VERTEX,{"disambiguationData":[OD(1.0)],"derivedFrom":[subQ1,subQ0]});Q79=makeQuery(id+"F0.imprint","IMPRINT",FACE,{"disambiguationData":[TD([[makeQuery(id+"F0.imprint","IMPRINT",EDGE,{"disambiguationData":[TD([[subQ2,-1.0]])],"derivedFrom":subQ1}),-1.0]])]});}
            var Q80;
            {var subQ0=sQuery(id+"F0.wireOp",EDGE,"E41.2.0");var subQ1=sQuery(id+"F0.wireOp",EDGE,"E35.2.1");var subQ2=makeQuery(id+"F0.imprint","INTERSECT",VERTEX,{"disambiguationData":[OD(1.0)],"derivedFrom":[subQ1,subQ0]});Q80=makeQuery(id+"F0.imprint","IMPRINT",FACE,{"disambiguationData":[TD([[makeQuery(id+"F0.imprint","IMPRINT",EDGE,{"disambiguationData":[TD([[subQ2,-1.0]])],"derivedFrom":subQ1}),1.0]])]});}
            var Q81;
            {var subQ0=sQuery(id+"F0.wireOp",EDGE,"E35.2.1");var subQ1=sQuery(id+"F0.wireOp",EDGE,"E35.1.9");var subQ2=makeQuery(id+"F0.imprint","INTERSECT",VERTEX,{"derivedFrom":[subQ1,subQ0]});Q81=makeQuery(id+"F0.imprint","IMPRINT",FACE,{"disambiguationData":[TD([[makeQuery(id+"F0.imprint","IMPRINT",EDGE,{"disambiguationData":[TD([[subQ2,-1.0]])],"derivedFrom":subQ1}),-1.0]])]});}
            extrude(context, id + "F1", {"entities" : qUnion([Q0, Q1, Q2, Q3, Q4, Q5, Q6, Q7, Q8, Q9, Q10, Q11, Q12, Q13, Q14, Q15, Q16, Q17, Q18, Q19, Q20, Q21, Q22, Q23, Q24, Q25, Q26, Q27, Q28, Q29, Q30, Q31, Q32, Q33, Q34, Q35, Q36, Q37, Q38, Q39, Q40, Q41, Q42, Q43, Q44, Q45, Q46, Q47, Q48, Q49, Q50, Q51, Q52, Q53, Q54, Q55, Q56, Q57, Q58, Q59, Q60, Q61, Q62, Q63, Q64, Q65, Q66, Q67, Q68, Q69, Q70, Q71, Q72, Q73, Q74, Q75, Q76, Q77, Q78, Q79, Q80, Q81]), "depth" : 6.35 * mm});
        }
    });
